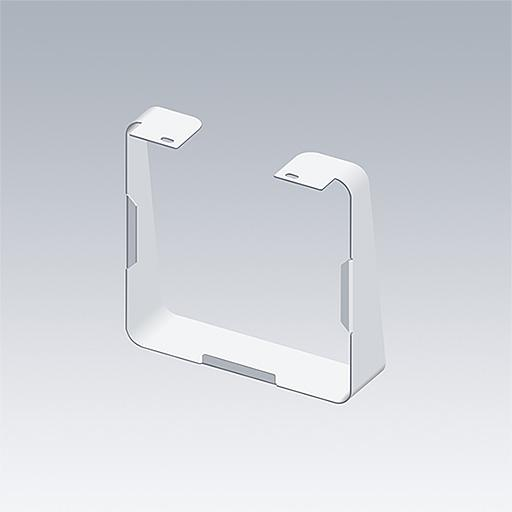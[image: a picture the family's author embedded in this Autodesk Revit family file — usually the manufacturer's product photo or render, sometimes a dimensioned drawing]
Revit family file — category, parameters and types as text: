
# Revit family: Thorn Caelon S12i
name_source: partatom
category: Lighting Fixtures
units: mm (PartAtom-declared; Revit-internal decimal feet)

## family parameters
Cut with Voids When Loaded = No
Host = Face
Light Source = No
Maintain Annotation Orientation = No
Part Type = Normal
Room Calculation Point = No
Round Connector Dimension = Use Diameter
Shared = No

## types (42) — shared parameters
Apparent Load = 20 VA
Assembly Code = Pr_70_70_48_75
Description = Outdoor flood and spotlight luminaires
Export Type to IFC As = IfcLightFixtureType
Has Cowl = No
Has Ground Spike = No
Lamp = LED
Luminaire Height = 210 mm  [stored 0.688976 ft]
Luminaire Length = 160 mm  [stored 0.524934 ft]
Luminaire Width = 149 mm  [stored 0.488845 ft]
Manufacturer = Thorn Lighting
Power Factor = 1
Type Accessory Cowl Black = Thorn CAELON-Accessory-S12i_S20i_S30i : CAELON S COWL/BK
Type Accessory Cowl White = Thorn CAELON-Accessory-S12i_S20i_S30i : CAELON S COWL/WH
Type Accessory Ground Spike Black = Thorn CAELON-Accessory-S12i_S20i_S30i : CAELON S12/20/30 GROUND SPIKE
Type Bracket Black = Thorn-Parts-CAELON-Bracket-S12l : Black
Type Bracket White = Thorn-Parts-CAELON-Bracket-S12l : White
Type Housing Black = Thorn-Parts-CAELON-Housing-S12l : Black
Type Housing White = Thorn-Parts-CAELON-Housing-S12l : White
Type IFC Predefined Type = DIRECTIONSOURCE
URL = https://www.thornlighting.com
zero-valued in all types: Default Elevation

## per-type parameters (varying)
| type | Housing Finish Black | Housing Finish White | Model | Optic | Type Accessory Cowl | Type Bracket | Type Housing | Type Image | Type Light Source |
| CAELON S12I 1200-827 M BK 66 HF | Yes | No | 21035546 | Medium | Thorn CAELON-Accessory-S12i_S20i_S30i : CAELON S COWL/BK | Thorn-Parts-CAELON-Bracket-S12l : Black | Thorn-Parts-CAELON-Housing-S12l : Black | TLG_CAEL_F_S12i-S20i-S30i_BK.png | Thorn-Light Sources-CAELON S12I : CAELON S12I 1200-827 M BK 66 HF_photometric_data |
| CAELON S12I 1200-827 M BK HL 66 HF | Yes | No | 21035543 | Medium | Thorn CAELON-Accessory-S12i_S20i_S30i : CAELON S COWL/BK | Thorn-Parts-CAELON-Bracket-S12l : Black | Thorn-Parts-CAELON-Housing-S12l : Black | TLG_CAEL_F_S12i-S20i-S30i_BK.png | Thorn-Light Sources-CAELON S12I : CAELON S12I 1200-827 M BK HL 66 HF_photometric_data |
| CAELON S12I 1200-827 M WH 66 HF | No | Yes | 21035552 | Medium | Thorn CAELON-Accessory-S12i_S20i_S30i : CAELON S COWL/WH | Thorn-Parts-CAELON-Bracket-S12l : White | Thorn-Parts-CAELON-Housing-S12l : White | TLG_CAEL_F_S12i-S20i-S30i_WH.png | Thorn-Light Sources-CAELON S12I : CAELON S12I 1200-827 M WH 66 HF_photometric_data |
| CAELON S12I 1200-827 M WH HL 66 HF | No | Yes | 21035549 | Medium | Thorn CAELON-Accessory-S12i_S20i_S30i : CAELON S COWL/WH | Thorn-Parts-CAELON-Bracket-S12l : White | Thorn-Parts-CAELON-Housing-S12l : White | TLG_CAEL_F_S12i-S20i-S30i_WH.png | Thorn-Light Sources-CAELON S12I : CAELON S12I 1200-827 M WH HL 66 HF_photometric_data |
| CAELON S12I 1200-827 N BK 66 HF | Yes | No | 21033980 | Narrow | Thorn CAELON-Accessory-S12i_S20i_S30i : CAELON S COWL/BK | Thorn-Parts-CAELON-Bracket-S12l : Black | Thorn-Parts-CAELON-Housing-S12l : Black | TLG_CAEL_F_S12i-S20i-S30i_BK.png | Thorn-Light Sources-CAELON S12I : CAELON S12I 1200-827 N BK 66 HF_photometric_data |
| CAELON S12I 1200-827 N BK HL 66 HF | Yes | No | 21033977 | Narrow | Thorn CAELON-Accessory-S12i_S20i_S30i : CAELON S COWL/BK | Thorn-Parts-CAELON-Bracket-S12l : Black | Thorn-Parts-CAELON-Housing-S12l : Black | TLG_CAEL_F_S12i-S20i-S30i_BK.png | Thorn-Light Sources-CAELON S12I : CAELON S12I 1200-827 N BK HL 66 HF_photometric_data |
| CAELON S12I 1200-827 N WH 66 HF | No | Yes | 21033986 | Narrow | Thorn CAELON-Accessory-S12i_S20i_S30i : CAELON S COWL/WH | Thorn-Parts-CAELON-Bracket-S12l : White | Thorn-Parts-CAELON-Housing-S12l : White | TLG_CAEL_F_S12i-S20i-S30i_WH.png | Thorn-Light Sources-CAELON S12I : CAELON S12I 1200-827 N WH 66 HF_photometric_data |
| CAELON S12I 1200-827 N WH HL 66 HF | No | Yes | 21033983 | Narrow | Thorn CAELON-Accessory-S12i_S20i_S30i : CAELON S COWL/WH | Thorn-Parts-CAELON-Bracket-S12l : White | Thorn-Parts-CAELON-Housing-S12l : White | TLG_CAEL_F_S12i-S20i-S30i_WH.png | Thorn-Light Sources-CAELON S12I : CAELON S12I 1200-827 N WH HL 66 HF_photometric_data |
| CAELON S12I 1200-827 SN BK 66 HF | Yes | No | 21033968 | Super Narrow | Thorn CAELON-Accessory-S12i_S20i_S30i : CAELON S COWL/BK | Thorn-Parts-CAELON-Bracket-S12l : Black | Thorn-Parts-CAELON-Housing-S12l : Black | TLG_CAEL_F_S12i-S20i-S30i_BK.png | Thorn-Light Sources-CAELON S12I : CAELON S12I 1200-827 SN BK 66 HF_photometric_data |
| CAELON S12I 1200-827 SN BK HL 66 HF | Yes | No | 21033965 | Super Narrow | Thorn CAELON-Accessory-S12i_S20i_S30i : CAELON S COWL/BK | Thorn-Parts-CAELON-Bracket-S12l : Black | Thorn-Parts-CAELON-Housing-S12l : Black | TLG_CAEL_F_S12i-S20i-S30i_BK.png | Thorn-Light Sources-CAELON S12I : CAELON S12I 1200-827 SN BK HL 66 HF_photometric_data |
| CAELON S12I 1200-827 SN WH 66 HF | No | Yes | 21033974 | Super Narrow | Thorn CAELON-Accessory-S12i_S20i_S30i : CAELON S COWL/WH | Thorn-Parts-CAELON-Bracket-S12l : White | Thorn-Parts-CAELON-Housing-S12l : White | TLG_CAEL_F_S12i-S20i-S30i_WH.png | Thorn-Light Sources-CAELON S12I : CAELON S12I 1200-827 SN WH 66 HF_photometric_data |
| CAELON S12I 1200-827 SN WH HL 66 HF | No | Yes | 21033971 | Super Narrow | Thorn CAELON-Accessory-S12i_S20i_S30i : CAELON S COWL/WH | Thorn-Parts-CAELON-Bracket-S12l : White | Thorn-Parts-CAELON-Housing-S12l : White | TLG_CAEL_F_S12i-S20i-S30i_WH.png | Thorn-Light Sources-CAELON S12I : CAELON S12I 1200-827 SN WH HL 66 HF_photometric_data |
| CAELON S12I 1200-827 W BK 66 HF | Yes | No | 21033989 | Wide | Thorn CAELON-Accessory-S12i_S20i_S30i : CAELON S COWL/BK | Thorn-Parts-CAELON-Bracket-S12l : Black | Thorn-Parts-CAELON-Housing-S12l : Black | TLG_CAEL_F_S12i-S20i-S30i_BK.png | Thorn-Light Sources-CAELON S12I : CAELON S12I 1200-827 W BK 66 HF_photometric_data |
| CAELON S12I 1200-827 W WH 66 HF | No | Yes | 21033992 | Wide | Thorn CAELON-Accessory-S12i_S20i_S30i : CAELON S COWL/WH | Thorn-Parts-CAELON-Bracket-S12l : White | Thorn-Parts-CAELON-Housing-S12l : White | TLG_CAEL_F_S12i-S20i-S30i_WH.png | Thorn-Light Sources-CAELON S12I : CAELON S12I 1200-827 W WH 66 HF_photometric_data |
| CAELON S12I 1200-830 M BK 66 HF | Yes | No | 21035558 | Medium | Thorn CAELON-Accessory-S12i_S20i_S30i : CAELON S COWL/BK | Thorn-Parts-CAELON-Bracket-S12l : Black | Thorn-Parts-CAELON-Housing-S12l : Black | TLG_CAEL_F_S12i-S20i-S30i_BK.png | Thorn-Light Sources-CAELON S12I : CAELON S12I 1200-830 M BK 66 HF_photometric_data |
| CAELON S12I 1200-830 M BK HL 66 HF | Yes | No | 21035555 | Medium | Thorn CAELON-Accessory-S12i_S20i_S30i : CAELON S COWL/BK | Thorn-Parts-CAELON-Bracket-S12l : Black | Thorn-Parts-CAELON-Housing-S12l : Black | TLG_CAEL_F_S12i-S20i-S30i_BK.png | Thorn-Light Sources-CAELON S12I : CAELON S12I 1200-830 M BK HL 66 HF_photometric_data |
| CAELON S12I 1200-830 M WH 66 HF | No | Yes | 21035564 | Medium | Thorn CAELON-Accessory-S12i_S20i_S30i : CAELON S COWL/WH | Thorn-Parts-CAELON-Bracket-S12l : White | Thorn-Parts-CAELON-Housing-S12l : White | TLG_CAEL_F_S12i-S20i-S30i_WH.png | Thorn-Light Sources-CAELON S12I : CAELON S12I 1200-830 M WH 66 HF_photometric_data |
| CAELON S12I 1200-830 M WH HL 66 HF | No | Yes | 21035561 | Medium | Thorn CAELON-Accessory-S12i_S20i_S30i : CAELON S COWL/WH | Thorn-Parts-CAELON-Bracket-S12l : White | Thorn-Parts-CAELON-Housing-S12l : White | TLG_CAEL_F_S12i-S20i-S30i_WH.png | Thorn-Light Sources-CAELON S12I : CAELON S12I 1200-830 M WH HL 66 HF_photometric_data |
| CAELON S12I 1200-830 N BK 66 HF | Yes | No | 21034012 | Narrow | Thorn CAELON-Accessory-S12i_S20i_S30i : CAELON S COWL/BK | Thorn-Parts-CAELON-Bracket-S12l : Black | Thorn-Parts-CAELON-Housing-S12l : Black | TLG_CAEL_F_S12i-S20i-S30i_BK.png | Thorn-Light Sources-CAELON S12I : CAELON S12I 1200-830 N BK 66 HF_photometric_data |
| CAELON S12I 1200-830 N BK HL 66 HF | Yes | No | 21034009 | Narrow | Thorn CAELON-Accessory-S12i_S20i_S30i : CAELON S COWL/BK | Thorn-Parts-CAELON-Bracket-S12l : Black | Thorn-Parts-CAELON-Housing-S12l : Black | TLG_CAEL_F_S12i-S20i-S30i_BK.png | Thorn-Light Sources-CAELON S12I : CAELON S12I 1200-830 N BK HL 66 HF_photometric_data |
| CAELON S12I 1200-830 N WH 66 HF | No | Yes | 21034018 | Narrow | Thorn CAELON-Accessory-S12i_S20i_S30i : CAELON S COWL/WH | Thorn-Parts-CAELON-Bracket-S12l : White | Thorn-Parts-CAELON-Housing-S12l : White | TLG_CAEL_F_S12i-S20i-S30i_WH.png | Thorn-Light Sources-CAELON S12I : CAELON S12I 1200-830 N WH 66 HF_photometric_data |
| CAELON S12I 1200-830 N WH HL 66 HF | No | Yes | 21034015 | Narrow | Thorn CAELON-Accessory-S12i_S20i_S30i : CAELON S COWL/WH | Thorn-Parts-CAELON-Bracket-S12l : White | Thorn-Parts-CAELON-Housing-S12l : White | TLG_CAEL_F_S12i-S20i-S30i_WH.png | Thorn-Light Sources-CAELON S12I : CAELON S12I 1200-830 N WH HL 66 HF_photometric_data |
| CAELON S12I 1200-830 SN BK 66 HF | Yes | No | 21034000 | Super Narrow | Thorn CAELON-Accessory-S12i_S20i_S30i : CAELON S COWL/BK | Thorn-Parts-CAELON-Bracket-S12l : Black | Thorn-Parts-CAELON-Housing-S12l : Black | TLG_CAEL_F_S12i-S20i-S30i_BK.png | Thorn-Light Sources-CAELON S12I : CAELON S12I 1200-830 SN BK 66 HF_photometric_data |
| CAELON S12I 1200-830 SN BK HL 66 HF | Yes | No | 21033997 | Super Narrow | Thorn CAELON-Accessory-S12i_S20i_S30i : CAELON S COWL/BK | Thorn-Parts-CAELON-Bracket-S12l : Black | Thorn-Parts-CAELON-Housing-S12l : Black | TLG_CAEL_F_S12i-S20i-S30i_BK.png | Thorn-Light Sources-CAELON S12I : CAELON S12I 1200-830 SN BK HL 66 HF_photometric_data |
| CAELON S12I 1200-830 SN WH 66 HF | No | Yes | 21034006 | Super Narrow | Thorn CAELON-Accessory-S12i_S20i_S30i : CAELON S COWL/WH | Thorn-Parts-CAELON-Bracket-S12l : White | Thorn-Parts-CAELON-Housing-S12l : White | TLG_CAEL_F_S12i-S20i-S30i_WH.png | Thorn-Light Sources-CAELON S12I : CAELON S12I 1200-830 SN WH 66 HF_photometric_data |
| CAELON S12I 1200-830 SN WH HL 66 HF | No | Yes | 21034003 | Super Narrow | Thorn CAELON-Accessory-S12i_S20i_S30i : CAELON S COWL/WH | Thorn-Parts-CAELON-Bracket-S12l : White | Thorn-Parts-CAELON-Housing-S12l : White | TLG_CAEL_F_S12i-S20i-S30i_WH.png | Thorn-Light Sources-CAELON S12I : CAELON S12I 1200-830 SN WH HL 66 HF_photometric_data |
| CAELON S12I 1200-830 W BK 66 HF | Yes | No | 21034021 | Wide | Thorn CAELON-Accessory-S12i_S20i_S30i : CAELON S COWL/BK | Thorn-Parts-CAELON-Bracket-S12l : Black | Thorn-Parts-CAELON-Housing-S12l : Black | TLG_CAEL_F_S12i-S20i-S30i_BK.png | Thorn-Light Sources-CAELON S12I : CAELON S12I 1200-830 W BK 66 HF_photometric_data |
| CAELON S12I 1200-830 W WH 66 HF | No | Yes | 21034024 | Wide | Thorn CAELON-Accessory-S12i_S20i_S30i : CAELON S COWL/WH | Thorn-Parts-CAELON-Bracket-S12l : White | Thorn-Parts-CAELON-Housing-S12l : White | TLG_CAEL_F_S12i-S20i-S30i_WH.png | Thorn-Light Sources-CAELON S12I : CAELON S12I 1200-830 W WH 66 HF_photometric_data |
| CAELON S12I 1200-840 M BK 66 HF | Yes | No | 21035570 | Medium | Thorn CAELON-Accessory-S12i_S20i_S30i : CAELON S COWL/BK | Thorn-Parts-CAELON-Bracket-S12l : Black | Thorn-Parts-CAELON-Housing-S12l : Black | TLG_CAEL_F_S12i-S20i-S30i_BK.png | Thorn-Light Sources-CAELON S12I : CAELON S12I 1200-840 M BK 66 HF_photometric_data |
| CAELON S12I 1200-840 M BK HL 66 HF | Yes | No | 21035567 | Medium | Thorn CAELON-Accessory-S12i_S20i_S30i : CAELON S COWL/BK | Thorn-Parts-CAELON-Bracket-S12l : Black | Thorn-Parts-CAELON-Housing-S12l : Black | TLG_CAEL_F_S12i-S20i-S30i_BK.png | Thorn-Light Sources-CAELON S12I : CAELON S12I 1200-840 M BK HL 66 HF_photometric_data |
| CAELON S12I 1200-840 M WH 66 HF | No | Yes | 21035576 | Medium | Thorn CAELON-Accessory-S12i_S20i_S30i : CAELON S COWL/WH | Thorn-Parts-CAELON-Bracket-S12l : White | Thorn-Parts-CAELON-Housing-S12l : White | TLG_CAEL_F_S12i-S20i-S30i_WH.png | Thorn-Light Sources-CAELON S12I : CAELON S12I 1200-840 M WH 66 HF_photometric_data |
| CAELON S12I 1200-840 M WH HL 66 HF | No | Yes | 21035573 | Medium | Thorn CAELON-Accessory-S12i_S20i_S30i : CAELON S COWL/WH | Thorn-Parts-CAELON-Bracket-S12l : White | Thorn-Parts-CAELON-Housing-S12l : White | TLG_CAEL_F_S12i-S20i-S30i_WH.png | Thorn-Light Sources-CAELON S12I : CAELON S12I 1200-840 M WH HL 66 HF_photometric_data |
| CAELON S12I 1200-840 N BK 66 HF | Yes | No | 21034044 | Narrow | Thorn CAELON-Accessory-S12i_S20i_S30i : CAELON S COWL/BK | Thorn-Parts-CAELON-Bracket-S12l : Black | Thorn-Parts-CAELON-Housing-S12l : Black | TLG_CAEL_F_S12i-S20i-S30i_BK.png | Thorn-Light Sources-CAELON S12I : CAELON S12I 1200-840 N BK 66 HF_photometric_data |
| CAELON S12I 1200-840 N BK HL 66 HF | Yes | No | 21034041 | Narrow | Thorn CAELON-Accessory-S12i_S20i_S30i : CAELON S COWL/BK | Thorn-Parts-CAELON-Bracket-S12l : Black | Thorn-Parts-CAELON-Housing-S12l : Black | TLG_CAEL_F_S12i-S20i-S30i_BK.png | Thorn-Light Sources-CAELON S12I : CAELON S12I 1200-840 N BK HL 66 HF_photometric_data |
| CAELON S12I 1200-840 N WH 66 HF | No | Yes | 21034050 | Narrow | Thorn CAELON-Accessory-S12i_S20i_S30i : CAELON S COWL/WH | Thorn-Parts-CAELON-Bracket-S12l : White | Thorn-Parts-CAELON-Housing-S12l : White | TLG_CAEL_F_S12i-S20i-S30i_WH.png | Thorn-Light Sources-CAELON S12I : CAELON S12I 1200-840 N WH 66 HF_photometric_data |
| CAELON S12I 1200-840 N WH HL 66 HF | No | Yes | 21034047 | Narrow | Thorn CAELON-Accessory-S12i_S20i_S30i : CAELON S COWL/WH | Thorn-Parts-CAELON-Bracket-S12l : White | Thorn-Parts-CAELON-Housing-S12l : White | TLG_CAEL_F_S12i-S20i-S30i_WH.png | Thorn-Light Sources-CAELON S12I : CAELON S12I 1200-840 N WH HL 66 HF_photometric_data |
| CAELON S12I 1200-840 SN BK 66 HF | Yes | No | 21034032 | Super Narrow | Thorn CAELON-Accessory-S12i_S20i_S30i : CAELON S COWL/BK | Thorn-Parts-CAELON-Bracket-S12l : Black | Thorn-Parts-CAELON-Housing-S12l : Black | TLG_CAEL_F_S12i-S20i-S30i_BK.png | Thorn-Light Sources-CAELON S12I : CAELON S12I 1200-840 SN BK 66 HF_photometric_data |
| CAELON S12I 1200-840 SN BK HL 66 HF | Yes | No | 21034029 | Super Narrow | Thorn CAELON-Accessory-S12i_S20i_S30i : CAELON S COWL/BK | Thorn-Parts-CAELON-Bracket-S12l : Black | Thorn-Parts-CAELON-Housing-S12l : Black | TLG_CAEL_F_S12i-S20i-S30i_BK.png | Thorn-Light Sources-CAELON S12I : CAELON S12I 1200-840 SN BK HL 66 HF_photometric_data |
| CAELON S12I 1200-840 SN WH 66 HF | No | Yes | 21034038 | Super Narrow | Thorn CAELON-Accessory-S12i_S20i_S30i : CAELON S COWL/WH | Thorn-Parts-CAELON-Bracket-S12l : White | Thorn-Parts-CAELON-Housing-S12l : White | TLG_CAEL_F_S12i-S20i-S30i_WH.png | Thorn-Light Sources-CAELON S12I : CAELON S12I 1200-840 SN WH 66 HF_photometric_data |
| CAELON S12I 1200-840 SN WH HL 66 HF | No | Yes | 21034035 | Super Narrow | Thorn CAELON-Accessory-S12i_S20i_S30i : CAELON S COWL/WH | Thorn-Parts-CAELON-Bracket-S12l : White | Thorn-Parts-CAELON-Housing-S12l : White | TLG_CAEL_F_S12i-S20i-S30i_WH.png | Thorn-Light Sources-CAELON S12I : CAELON S12I 1200-840 SN WH HL 66 HF_photometric_data |
| CAELON S12I 1200-840 W BK 66 HF | Yes | No | 21034053 | Wide | Thorn CAELON-Accessory-S12i_S20i_S30i : CAELON S COWL/BK | Thorn-Parts-CAELON-Bracket-S12l : Black | Thorn-Parts-CAELON-Housing-S12l : Black | TLG_CAEL_F_S12i-S20i-S30i_BK.png | Thorn-Light Sources-CAELON S12I : CAELON S12I 1200-840 W BK 66 HF_photometric_data |
| CAELON S12I 1200-840 W WH 66 HF | No | Yes | 21034056 | Wide | Thorn CAELON-Accessory-S12i_S20i_S30i : CAELON S COWL/WH | Thorn-Parts-CAELON-Bracket-S12l : White | Thorn-Parts-CAELON-Housing-S12l : White | TLG_CAEL_F_S12i-S20i-S30i_WH.png | Thorn-Light Sources-CAELON S12I : CAELON S12I 1200-840 W WH 66 HF_photometric_data |

note: [stored X ft] marks values corroborated as IEEE doubles in the binary element streams (Revit-internal decimal feet)

## geometry (parser evidence)
native form markers: Sweep x14
no freeform markers — native parametric forms only
